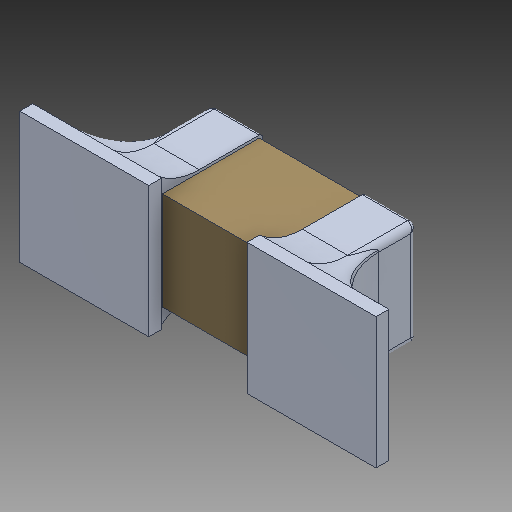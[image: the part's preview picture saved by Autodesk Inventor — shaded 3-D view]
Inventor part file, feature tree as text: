
AUTODESK INVENTOR PART (.ipt)
format: ipt  version: 2018 (Build 220112000, 112)  size: 208,384 bytes
history: native  units: mm
features: fillet x1
ambient origin geometry x8: Origin, YZ Plane, XZ Plane, XY Plane, X Axis, Y Axis, Z Axis, Center Point
bodies: Volumenkörper1 (feature_tree)
feature tree (1):
  fillet  "Fillet5"  [1 undecoded]
note: 1 required parameter value undecoded (feature->parameter linkage not recoverable at this tier; creation-order binding heuristic only, values carry confidence <= 0.55)
